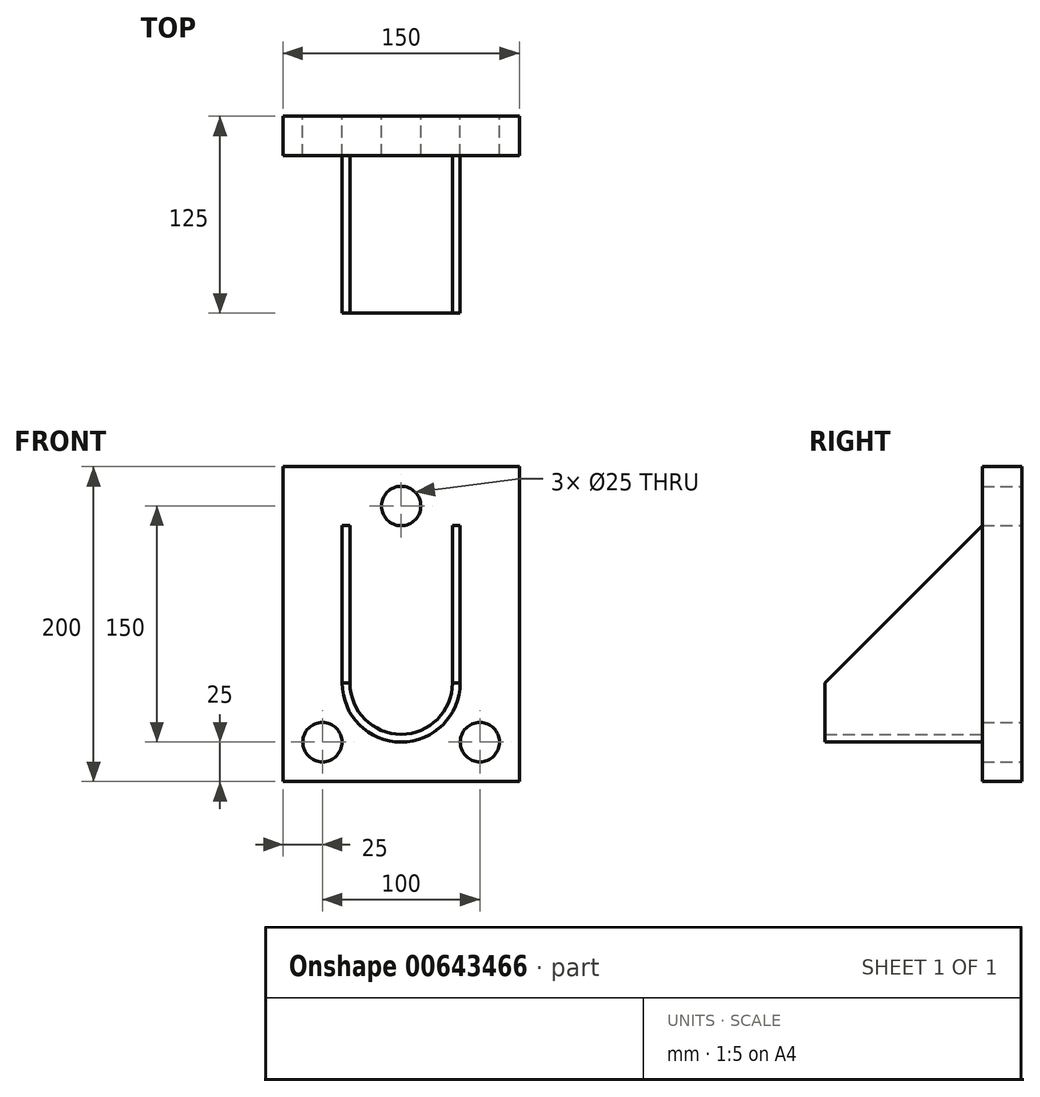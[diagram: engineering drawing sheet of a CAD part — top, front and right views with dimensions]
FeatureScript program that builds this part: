
annotation { "Feature Type Name" : "Feature", "Feature Type Description" : "" }
export const myFeature = defineFeature(function(context is Context, id is Id, definition is map)
    precondition{}
    {
        {
            var Q0;
            Q0=qCreatedBy(makeId("Front.planeOp"),FACE);
            var sketch = newSketch(context, id + "F0", { "sketchPlane" : qUnion([Q0])});
            skLineSegment(sketch, "E0.bottom", {"start": v(0, 0) * mm, "end": v(150, 0) * mm});
            skLineSegment(sketch, "E0.top", {"start": v(0, -200) * mm, "end": v(150, -200) * mm});
            skLineSegment(sketch, "E0.left", {"start": v(0, 0) * mm, "end": v(0, -200) * mm});
            skLineSegment(sketch, "E0.right", {"start": v(150, 0) * mm, "end": v(150, -200) * mm});
            skCircle(sketch, "E1", {"center": v(75, -25) * mm, "radius": 12.5 * mm});
            skPoint(sketch, "E1.centerSnap0", {"position": v(75, 0) * mm});
            skCircle(sketch, "E2", {"center": v(25, -175) * mm, "radius": 12.5 * mm});
            skCircle(sketch, "E3", {"center": v(125, -175) * mm, "radius": 12.5 * mm});
            skSolve(sketch);
        }
        {
            var Q0;
            Q0 = qSketchRegion(id + "F0", true);
            extrude(context, id + "F1", {"entities" : qUnion([Q0]), "depth" : 25 * mm, "offsetDistance" : 25 * mm});
        }
        {
            var Q0;
            Q0=makeQuery(id+"F1.opExtrude","CAP_FACE",FACE,{"disambiguationData":[OSD([sQuery(id+"F0.wireOp",EDGE,"E0.bottom"),sQuery(id+"F0.wireOp",EDGE,"E0.top"),sQuery(id+"F0.wireOp",EDGE,"E0.left"),sQuery(id+"F0.wireOp",EDGE,"E0.right"),sQuery(id+"F0.wireOp",EDGE,"E1"),sQuery(id+"F0.wireOp",EDGE,"E2"),sQuery(id+"F0.wireOp",EDGE,"E3")])],"isStart":false});
            var sketch = newSketch(context, id + "F2", { "sketchPlane" : qUnion([Q0])});
            skArc(sketch, "E4", {"start": v(37.5, -137.5) * mm, "mid": v(75, -175) * mm, "end": v(112.5, -137.5) * mm});
            skPoint(sketch, "E4.centerSnap0", {"position": v(75, -200) * mm});
            skArc(sketch, "E5", {"start": v(42.5, -137.5) * mm, "mid": v(75, -170) * mm, "end": v(107.5, -137.5) * mm});
            skPoint(sketch, "E6", {"position": v(75, -175) * mm});
            skLineSegment(sketch, "E7", {"start": v(37.5, -137.5) * mm, "end": v(42.5, -137.5) * mm});
            skLineSegment(sketch, "E8.trimOffspring", {"start": v(107.5, -137.5) * mm, "end": v(112.5, -137.5) * mm});
            skSolve(sketch);
        }
        {
            var Q0;
            Q0 = qSketchRegion(id + "F2", true);
            extrude(context, id + "F3", {"entities" : qUnion([Q0]), "operationType" : NewBodyOperationType.ADD, "depth" : 100 * mm, "offsetDistance" : 25 * mm});
        }
        {
            var Q0;
            Q0=makeQuery(id+"F3.opExtrude","SWEPT_FACE",FACE,{"disambiguationData":[OSD([sQuery(id+"F2.wireOp",EDGE,"E8.trimOffspring")])]});
            var sketch = newSketch(context, id + "F4", { "sketchPlane" : qUnion([Q0])});
            skLineSegment(sketch, "E9.bottom", {"start": v(107.5, -25) * mm, "end": v(112.5, -25) * mm});
            skLineSegment(sketch, "E9.top", {"start": v(107.5, -125) * mm, "end": v(112.5, -125) * mm});
            skLineSegment(sketch, "E9.left", {"start": v(107.5, -25) * mm, "end": v(107.5, -125) * mm});
            skLineSegment(sketch, "E9.right", {"start": v(112.5, -25) * mm, "end": v(112.5, -125) * mm});
            skSolve(sketch);
        }
        {
            var Q0;
            Q0 = qSketchRegion(id + "F4", true);
            extrude(context, id + "F5", {"entities" : qUnion([Q0]), "operationType" : NewBodyOperationType.ADD, "depth" : 100 * mm, "offsetDistance" : 25 * mm});
        }
        {
            var Q0;
            Q0=makeQuery(id+"F5.opExtrude","SWEPT_FACE",FACE,{"disambiguationData":[OSD([sQuery(id+"F4.wireOp",EDGE,"E9.right")])]});
            var sketch = newSketch(context, id + "F6", { "sketchPlane" : qUnion([Q0])});
            skLineSegment(sketch, "E10", {"start": v(-125, -137.5) * mm, "end": v(-25, -37.5) * mm});
            skSolve(sketch);
        }
        {
            var Q0;
            Q0=makeQuery(id+"F6.imprint","IMPRINT",FACE,{"disambiguationData":[TD([[makeQuery(id+"F6.imprint","IMPRINT",EDGE,{"derivedFrom":sQuery(id+"F6.wireOp",EDGE,"E10")}),1.0]])]});
            extrude(context, id + "F7", {"entities" : qUnion([Q0]), "operationType" : NewBodyOperationType.REMOVE, "oppositeDirection" : true, "depth" : 25 * mm, "offsetDistance" : 25 * mm});
        }
        {
            var Q0;
            Q0=makeQuery(id+"F3.opExtrude","SWEPT_FACE",FACE,{"disambiguationData":[OSD([sQuery(id+"F2.wireOp",EDGE,"E7")])]});
            var sketch = newSketch(context, id + "F8", { "sketchPlane" : qUnion([Q0])});
            skLineSegment(sketch, "E11.bottom", {"start": v(37.5, -25) * mm, "end": v(42.5, -25) * mm});
            skLineSegment(sketch, "E11.top", {"start": v(37.5, -125) * mm, "end": v(42.5, -125) * mm});
            skLineSegment(sketch, "E11.left", {"start": v(37.5, -25) * mm, "end": v(37.5, -125) * mm});
            skLineSegment(sketch, "E11.right", {"start": v(42.5, -25) * mm, "end": v(42.5, -125) * mm});
            skSolve(sketch);
        }
        {
            var Q0;
            Q0 = qSketchRegion(id + "F8", true);
            extrude(context, id + "F9", {"entities" : qUnion([Q0]), "operationType" : NewBodyOperationType.ADD, "depth" : 100 * mm, "offsetDistance" : 25 * mm});
        }
        {
            var Q0;
            Q0=makeQuery(id+"F9.opExtrude","SWEPT_FACE",FACE,{"disambiguationData":[OSD([sQuery(id+"F8.wireOp",EDGE,"E11.right")])]});
            var sketch = newSketch(context, id + "F10", { "sketchPlane" : qUnion([Q0])});
            skLineSegment(sketch, "E12", {"start": v(-125, -137.5) * mm, "end": v(-25, -37.5) * mm});
            skSolve(sketch);
        }
        {
            var Q0;
            Q0=makeQuery(id+"F10.imprint","IMPRINT",FACE,{"disambiguationData":[TD([[makeQuery(id+"F10.imprint","IMPRINT",EDGE,{"derivedFrom":sQuery(id+"F10.wireOp",EDGE,"E12")}),1.0]])]});
            extrude(context, id + "F11", {"entities" : qUnion([Q0]), "operationType" : NewBodyOperationType.REMOVE, "oppositeDirection" : true, "depth" : 25 * mm, "offsetDistance" : 25 * mm});
        }
    });
